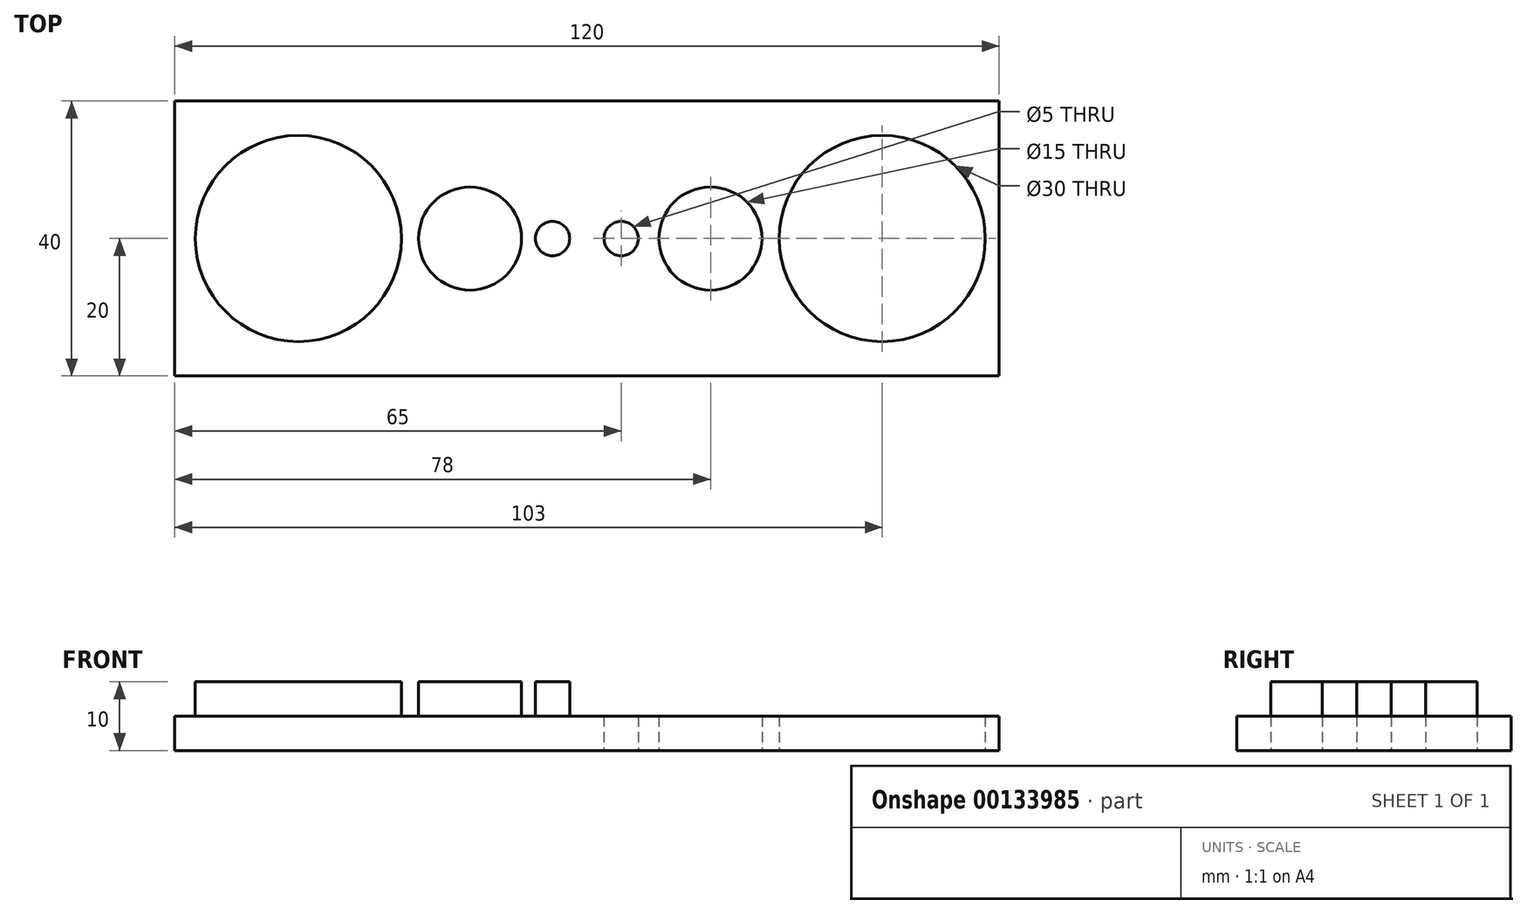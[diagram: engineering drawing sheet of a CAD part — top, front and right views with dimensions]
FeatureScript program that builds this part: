
annotation { "Feature Type Name" : "Feature", "Feature Type Description" : "" }
export const myFeature = defineFeature(function(context is Context, id is Id, definition is map)
    precondition{}
    {
        {
            var Q0;
            Q0=qCreatedBy(makeId("Top.planeOp"),FACE);
            var sketch = newSketch(context, id + "F0", { "sketchPlane" : qUnion([Q0])});
            skLineSegment(sketch, "E0.bottom", {"start": v(60, -20) * mm, "end": v(-60, -20) * mm});
            skLineSegment(sketch, "E0.top", {"start": v(60, 20) * mm, "end": v(-60, 20) * mm});
            skLineSegment(sketch, "E0.left", {"start": v(60, -20) * mm, "end": v(60, 20) * mm});
            skLineSegment(sketch, "E0.right", {"start": v(-60, -20) * mm, "end": v(-60, 20) * mm});
            skPoint(sketch, "E0.middle", {"position": v(0, 0) * mm});
            skCircle(sketch, "E1", {"center": v(5, 0) * mm, "radius": 2.5 * mm});
            skCircle(sketch, "E2", {"center": v(18, 0) * mm, "radius": 7.5 * mm});
            skCircle(sketch, "E3", {"center": v(43, 0) * mm, "radius": 15 * mm});
            skSolve(sketch);
        }
        {
            var Q0;
            Q0=makeQuery(id+"F0.imprint","IMPRINT",FACE,{"disambiguationData":[TD([[makeQuery(id+"F0.imprint","IMPRINT",EDGE,{"derivedFrom":sQuery(id+"F0.wireOp",EDGE,"E0.bottom")}),-1.0]])]});
            extrude(context, id + "F1", {"entities" : qUnion([Q0]), "depth" : 5 * mm, "offsetDistance" : 25 * mm});
        }
        {
            var Q0;
            Q0=makeQuery(id+"F1.opExtrude","CAP_FACE",FACE,{"disambiguationData":[OSD([sQuery(id+"F0.wireOp",EDGE,"E0.bottom"),sQuery(id+"F0.wireOp",EDGE,"E0.top"),sQuery(id+"F0.wireOp",EDGE,"E0.left"),sQuery(id+"F0.wireOp",EDGE,"E0.right"),sQuery(id+"F0.wireOp",EDGE,"E1"),sQuery(id+"F0.wireOp",EDGE,"E2"),sQuery(id+"F0.wireOp",EDGE,"E3")])],"isStart":false});
            var sketch = newSketch(context, id + "F2", { "sketchPlane" : qUnion([Q0])});
            skCircle(sketch, "E4", {"center": v(-5, 0) * mm, "radius": 2.5 * mm});
            skCircle(sketch, "E5", {"center": v(-17, 0) * mm, "radius": 7.5 * mm});
            skCircle(sketch, "E6", {"center": v(-42, 0) * mm, "radius": 15 * mm});
            skSolve(sketch);
        }
        {
            var Q0;
            Q0 = qSketchRegion(id + "F2", true);
            extrude(context, id + "F3", {"entities" : qUnion([Q0]), "operationType" : NewBodyOperationType.ADD, "depth" : 5 * mm, "offsetDistance" : 25 * mm});
        }
    });
